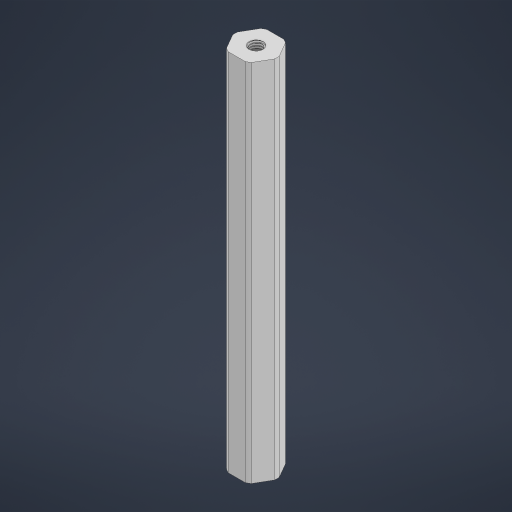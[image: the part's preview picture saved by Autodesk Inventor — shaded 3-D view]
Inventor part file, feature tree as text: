
AUTODESK INVENTOR PART (.ipt)
format: ipt  version: 2023 (Build 270158000, 158)  size: 1,018,880 bytes
history: native  units: in
note: dims shown in document units (in); Inventor stores cm internally (conversion verified against a paired STEP export)
features: mirror x1
ambient origin geometry x8: Origin, YZ Plane, XZ Plane, XY Plane, X Axis, Y Axis, Z Axis, Center Point
bodies: Solid1 (feature_tree)
feature tree (1):
  mirror  "Mirror2"
